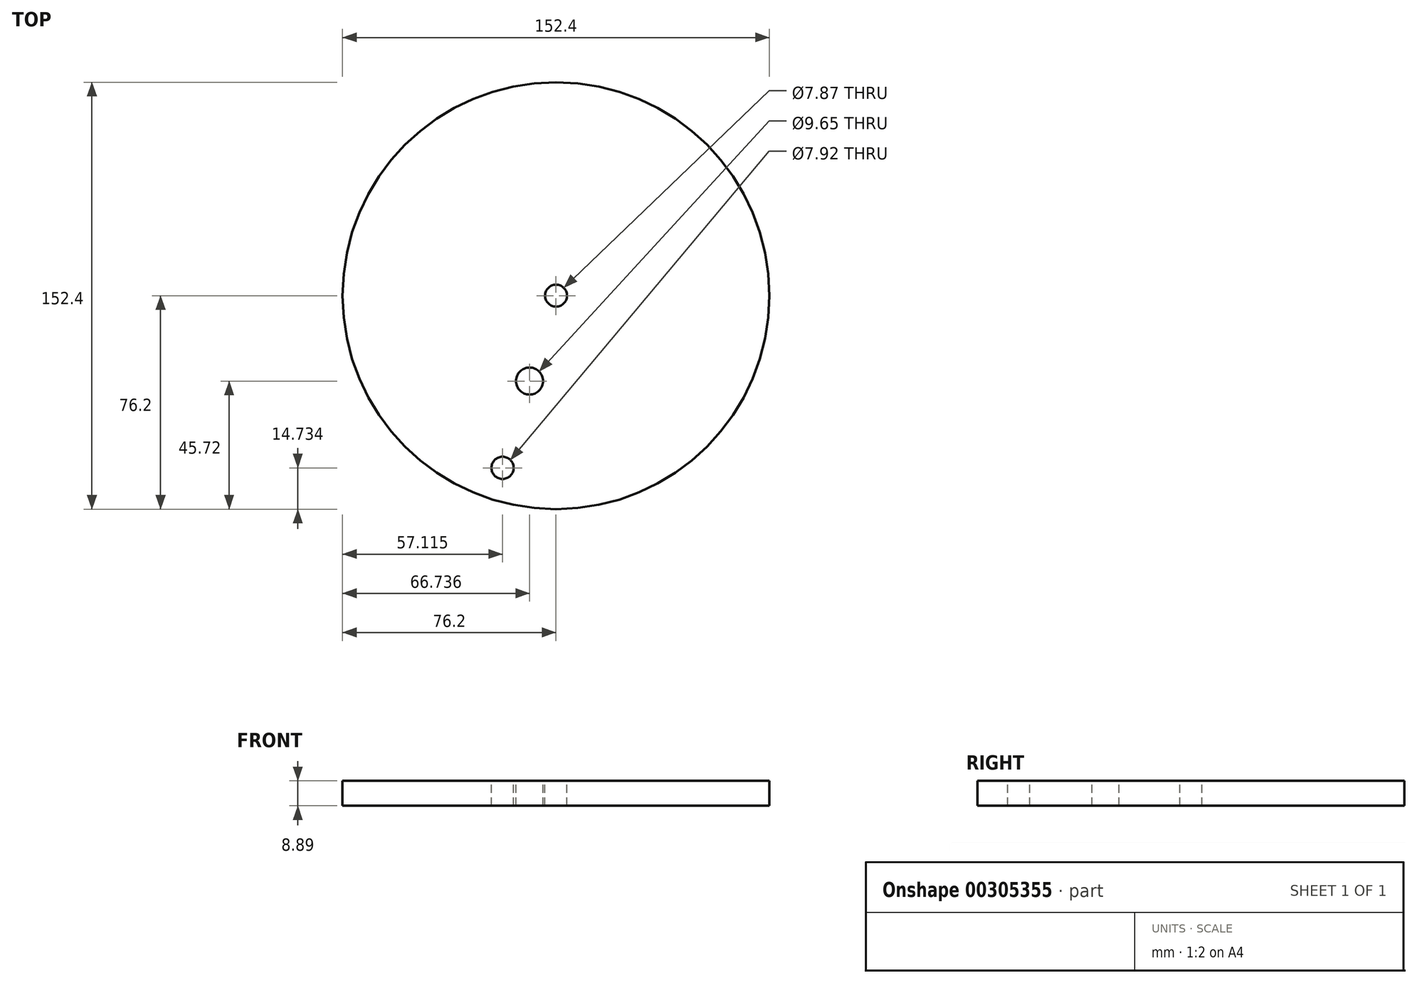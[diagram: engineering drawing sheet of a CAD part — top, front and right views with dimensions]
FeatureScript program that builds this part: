
annotation { "Feature Type Name" : "Feature", "Feature Type Description" : "" }
export const myFeature = defineFeature(function(context is Context, id is Id, definition is map)
    precondition{}
    {
        {
            var Q0;
            Q0=qCreatedBy(makeId("Top.planeOp"),FACE);
            var sketch = newSketch(context, id + "F0", { "sketchPlane" : qUnion([Q0])});
            skCircle(sketch, "E0", {"center": v(0, 0) * mm, "radius": 76.2 * mm});
            skSolve(sketch);
        }
        {
            var Q0;
            Q0=makeQuery(id+"F0.imprint","IMPRINT",FACE,{"disambiguationData":[TD([[makeQuery(id+"F0.imprint","IMPRINT",EDGE,{"derivedFrom":sQuery(id+"F0.wireOp",EDGE,"E0")}),1.0]])]});
            extrude(context, id + "F1", {"entities" : qUnion([Q0]), "depth" : 8.9 * mm});
        }
        {
            var Q0;
            Q0=makeQuery(id+"F1.opExtrude","CAP_FACE",FACE,{"disambiguationData":[OSD([sQuery(id+"F0.wireOp",EDGE,"E0")])],"isStart":false});
            var sketch = newSketch(context, id + "F2", { "sketchPlane" : qUnion([Q0])});
            skCircle(sketch, "E1", {"center": v(0, 0) * mm, "radius": 3.94 * mm});
            skSolve(sketch);
        }
        {
            var Q0;
            Q0=makeQuery(id+"F2.imprint","IMPRINT",FACE,{"disambiguationData":[TD([[makeQuery(id+"F2.imprint","IMPRINT",EDGE,{"derivedFrom":sQuery(id+"F2.wireOp",EDGE,"E1")}),1.0]])]});
            extrude(context, id + "F3", {"entities" : qUnion([Q0]), "operationType" : NewBodyOperationType.REMOVE, "oppositeDirection" : true, "depth" : 25.4 * mm});
        }
        {
            var Q0;
            Q0=makeQuery(id+"F1.opExtrude","CAP_FACE",FACE,{"disambiguationData":[OSD([sQuery(id+"F0.wireOp",EDGE,"E0")])],"isStart":false});
            var sketch = newSketch(context, id + "F4", { "sketchPlane" : qUnion([Q0])});
            skCircle(sketch, "E2", {"center": v(-9.46, -30.48) * mm, "radius": 4.83 * mm});
            skSolve(sketch);
        }
        {
            var Q0;
            Q0=makeQuery(id+"F4.imprint","IMPRINT",FACE,{"disambiguationData":[TD([[makeQuery(id+"F4.imprint","IMPRINT",EDGE,{"derivedFrom":sQuery(id+"F4.wireOp",EDGE,"E2")}),1.0]])]});
            extrude(context, id + "F5", {"entities" : qUnion([Q0]), "operationType" : NewBodyOperationType.REMOVE, "oppositeDirection" : true, "depth" : 25.4 * mm});
        }
        {
            var Q0;
            Q0=makeQuery(id+"F1.opExtrude","CAP_FACE",FACE,{"disambiguationData":[OSD([sQuery(id+"F0.wireOp",EDGE,"E0")])],"isStart":false});
            var sketch = newSketch(context, id + "F6", { "sketchPlane" : qUnion([Q0])});
            skCircle(sketch, "E3", {"center": v(-19.09, -61.47) * mm, "radius": 3.96 * mm});
            skSolve(sketch);
        }
        {
            var Q0;
            Q0=makeQuery(id+"F6.imprint","IMPRINT",FACE,{"disambiguationData":[TD([[makeQuery(id+"F6.imprint","IMPRINT",EDGE,{"derivedFrom":sQuery(id+"F6.wireOp",EDGE,"E3")}),1.0]])]});
            extrude(context, id + "F7", {"entities" : qUnion([Q0]), "operationType" : NewBodyOperationType.REMOVE, "oppositeDirection" : true, "depth" : 25.4 * mm});
        }
    });
